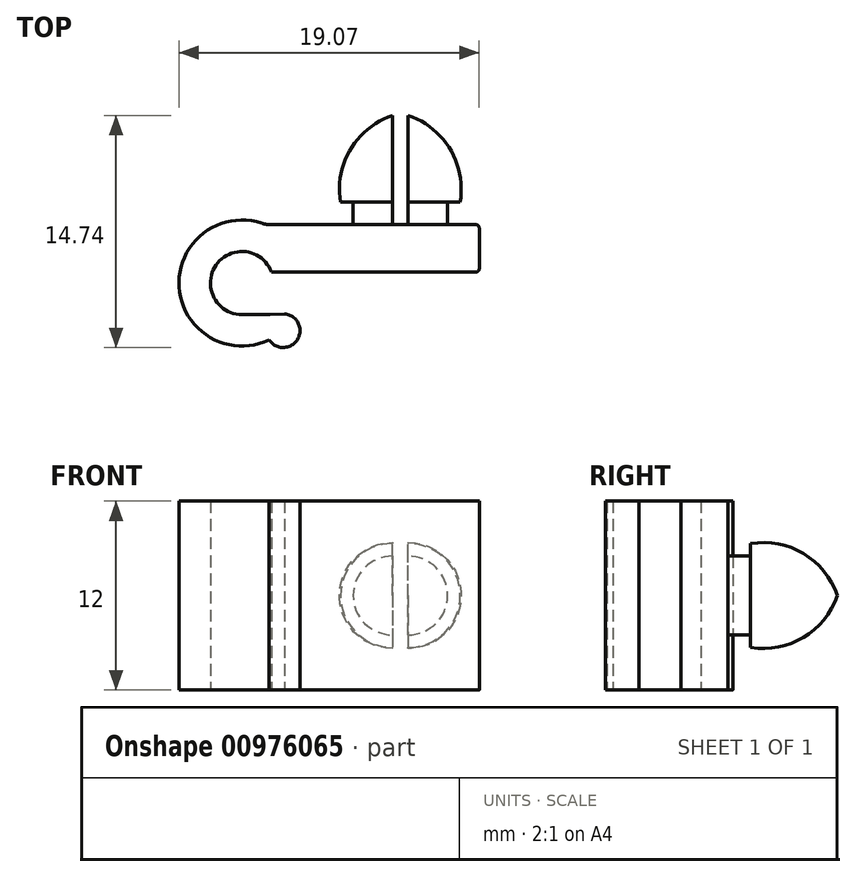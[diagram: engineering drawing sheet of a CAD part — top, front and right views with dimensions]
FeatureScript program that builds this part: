
annotation { "Feature Type Name" : "Feature", "Feature Type Description" : "" }
export const myFeature = defineFeature(function(context is Context, id is Id, definition is map)
    precondition{}
    {
        {
            var Q0;
            Q0=qCreatedBy(makeId("Top.planeOp"),FACE);
            var sketch = newSketch(context, id + "F0", { "sketchPlane" : qUnion([Q0])});
            skArc(sketch, "E0", {"start": v(1.87, 0.7) * mm, "mid": v(-1.64, 1.14) * mm, "end": v(0, -2) * mm});
            skArc(sketch, "E1.0", {"start": v(1.24, 3.8) * mm, "mid": v(-4, -0.27) * mm, "end": v(1.74, -3.6) * mm});
            skLineSegment(sketch, "E2", {"start": v(1.86, 3.7) * mm, "end": v(14.87, 3.7) * mm});
            skLineSegment(sketch, "E3", {"start": v(15.07, 3.5) * mm, "end": v(15.07, 0.9) * mm});
            skLineSegment(sketch, "E4", {"start": v(14.87, 0.7) * mm, "end": v(1.87, 0.7) * mm});
            skLineSegment(sketch, "E5", {"start": v(0, -2) * mm, "end": v(1.77, -2) * mm});
            skArc(sketch, "E6", {"start": v(1.71, -3.6) * mm, "mid": v(3.53, -3.59) * mm, "end": v(2.72, -1.96) * mm});
            skPoint(sketch, "E7.start.orphan", {"position": v(0, 0.7) * mm});
            skPoint(sketch, "E8.start.orphan", {"position": v(0, -4) * mm});
            skLineSegment(sketch, "E9", {"start": v(1.77, -2) * mm, "end": v(2.72, -1.96) * mm});
            skArc(sketch, "E10.filletArc", {"start": v(1.71, -3.6) * mm, "mid": v(1.73, -3.56) * mm, "end": v(1.74, -3.6) * mm});
            skPoint(sketch, "E11.visualSharp", {"position": v(1.51, 3.7) * mm});
            skArc(sketch, "E11.filletArc", {"start": v(1.24, 3.8) * mm, "mid": v(1.55, 3.73) * mm, "end": v(1.86, 3.7) * mm});
            skPoint(sketch, "E12.visualSharp", {"position": v(15.07, 3.7) * mm});
            skArc(sketch, "E12.filletArc", {"start": v(15.07, 3.5) * mm, "mid": v(15.01, 3.64) * mm, "end": v(14.87, 3.7) * mm});
            skPoint(sketch, "E13.visualSharp", {"position": v(15.07, 0.7) * mm});
            skArc(sketch, "E13.filletArc", {"start": v(14.87, 0.7) * mm, "mid": v(15.01, 0.76) * mm, "end": v(15.07, 0.9) * mm});
            skSolve(sketch);
        }
        {
            var Q0;
            Q0 = qSketchRegion(id + "F0", true);
            extrude(context, id + "F1", {"entities" : qUnion([Q0]), "endBound" : BoundingType.SYMMETRIC, "depth" : 12 * mm, "offsetDistance" : 25 * mm});
        }
        {
            var Q0;
            Q0=qCreatedBy(makeId("Top.planeOp"),FACE);
            var sketch = newSketch(context, id + "F2", { "sketchPlane" : qUnion([Q0])});
            skLineSegment(sketch, "E14", {"start": v(9.56, 3.64) * mm, "end": v(9.56, 10.64) * mm});
            skLineSegment(sketch, "E15", {"start": v(9.56, 3.64) * mm, "end": v(7.06, 3.64) * mm});
            skLineSegment(sketch, "E16", {"start": v(7.06, 3.64) * mm, "end": v(7.06, 5.14) * mm});
            skLineSegment(sketch, "E17", {"start": v(7.06, 5.14) * mm, "end": v(6.26, 5.14) * mm});
            skArc(sketch, "E18", {"start": v(9.56, 10.64) * mm, "mid": v(6.9, 8.5) * mm, "end": v(6.26, 5.14) * mm});
            skSolve(sketch);
        }
        {
            var Q0;
            Q0 = qSketchRegion(id + "F2", true);
            var Q1;
            Q1=sQuery(id+"F2.wireOp",EDGE,"E14");
            revolve(context, id + "F3", {"surfaceOperationType" : NewSurfaceOperationType.NEW, "entities" : qUnion([Q0]), "axis" : qUnion([Q1]), "revolveType" : RevolveType.SYMMETRIC, "angle" : 180 * degree});
        }
        {
            var Q0;
            Q0=makeQuery(id+"F3.opRevolve","CAP_FACE",FACE,{"disambiguationData":[OSD([sQuery(id+"F2.wireOp",EDGE,"E14"),sQuery(id+"F2.wireOp",EDGE,"E15"),sQuery(id+"F2.wireOp",EDGE,"E16"),sQuery(id+"F2.wireOp",EDGE,"E17"),sQuery(id+"F2.wireOp",EDGE,"E18")])],"isStart":false});
            cPlane(context, id + "F4", {"entities" : qUnion([Q0]), "cplaneType" : CPlaneType.OFFSET, "offset" : .5 * mm, "width" : 150 * mm, "height" : 150 * mm});
        }
        {
            var Q0;
            Q0=makeQuery(id+"F3.opRevolve","SWEPT_BODY",BODY,{"disambiguationData":[OSD([sQuery(id+"F2.wireOp",EDGE,"E14"),sQuery(id+"F2.wireOp",EDGE,"E15"),sQuery(id+"F2.wireOp",EDGE,"E16"),sQuery(id+"F2.wireOp",EDGE,"E17"),sQuery(id+"F2.wireOp",EDGE,"E18")])]});
            var Q1;
            Q1=qCreatedBy(id+"F4.planeOp",FACE);
            mirror(context, id + "F5", {"operationType" : NewBodyOperationType.ADD, "entities" : qUnion([Q0]), "mirrorPlane" : qUnion([Q1])});
        }
    });
